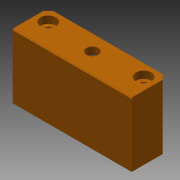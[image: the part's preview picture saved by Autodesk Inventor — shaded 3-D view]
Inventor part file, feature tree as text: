
AUTODESK INVENTOR PART (.ipt)
format: ipt  version: 2015 (Build 190159000, 159)  size: 130,560 bytes
history: native  units: mm
features: extrude x3, hole x3, sketch x3, chamfer x2
ambient origin geometry x8: Origin, YZ Plane, XZ Plane, XY Plane, X Axis, Y Axis, Z Axis, Center Point
bodies: Volumenkörper1 (feature_tree)
feature tree (11):
  extrude  "Extrusion1"  Depth=50.0mm
  hole  "Bohrung1"  [1 undecoded]
  hole  "Bohrung2"  [1 undecoded]
  chamfer  "Fase1"  Distance=10.0mm
  extrude  "Extrusion2"  Depth=2.0mm TaperAngle=0.0deg
  hole  "Bohrung3"  [1 undecoded]
  chamfer  "Fase2"  Distance=2.0mm Angle=45.0deg
  extrude  "Extrusion4"  Depth=2.0mm TaperAngle=0.0deg
  sketch  "Skizze1"  dims[d0=15.0mm d1=50.0mm]
  sketch  "Skizze2"  dims[d2=28.5mm d3=0.0mm]
  sketch  "Skizze4"  dims[d4=5.0mm d5=5.0mm d6=3.4mm d7=6.0mm d8=6.5mm d9=3.0mm d10=90.0deg d11=8.0mm d12=20.594885mm d13=5.0mm d14=5.0mm d15=3.4mm d16=6.0mm d17=6.5mm d18=3.0mm d19=90.0deg d20=8.0mm d21=20.594885mm d22=0.5mm d23=2.0mm d24=45.0deg d25=10.0mm d26=10.0mm d28=25.5mm d29=0.0mm d35=8.0mm d45=25.0mm d37=5.0mm d38=6.0mm d39=4.0mm d40=2.0mm d41=90.0deg d42=8.0mm d43=20.594885mm d44=2.0mm d46=2.0mm d47=2.0mm d48=45.0deg d49=1.5mm d50=0.0mm]
note: 3 required parameter values undecoded (feature->parameter linkage not recoverable at this tier; creation-order binding heuristic only, values carry confidence <= 0.55)
